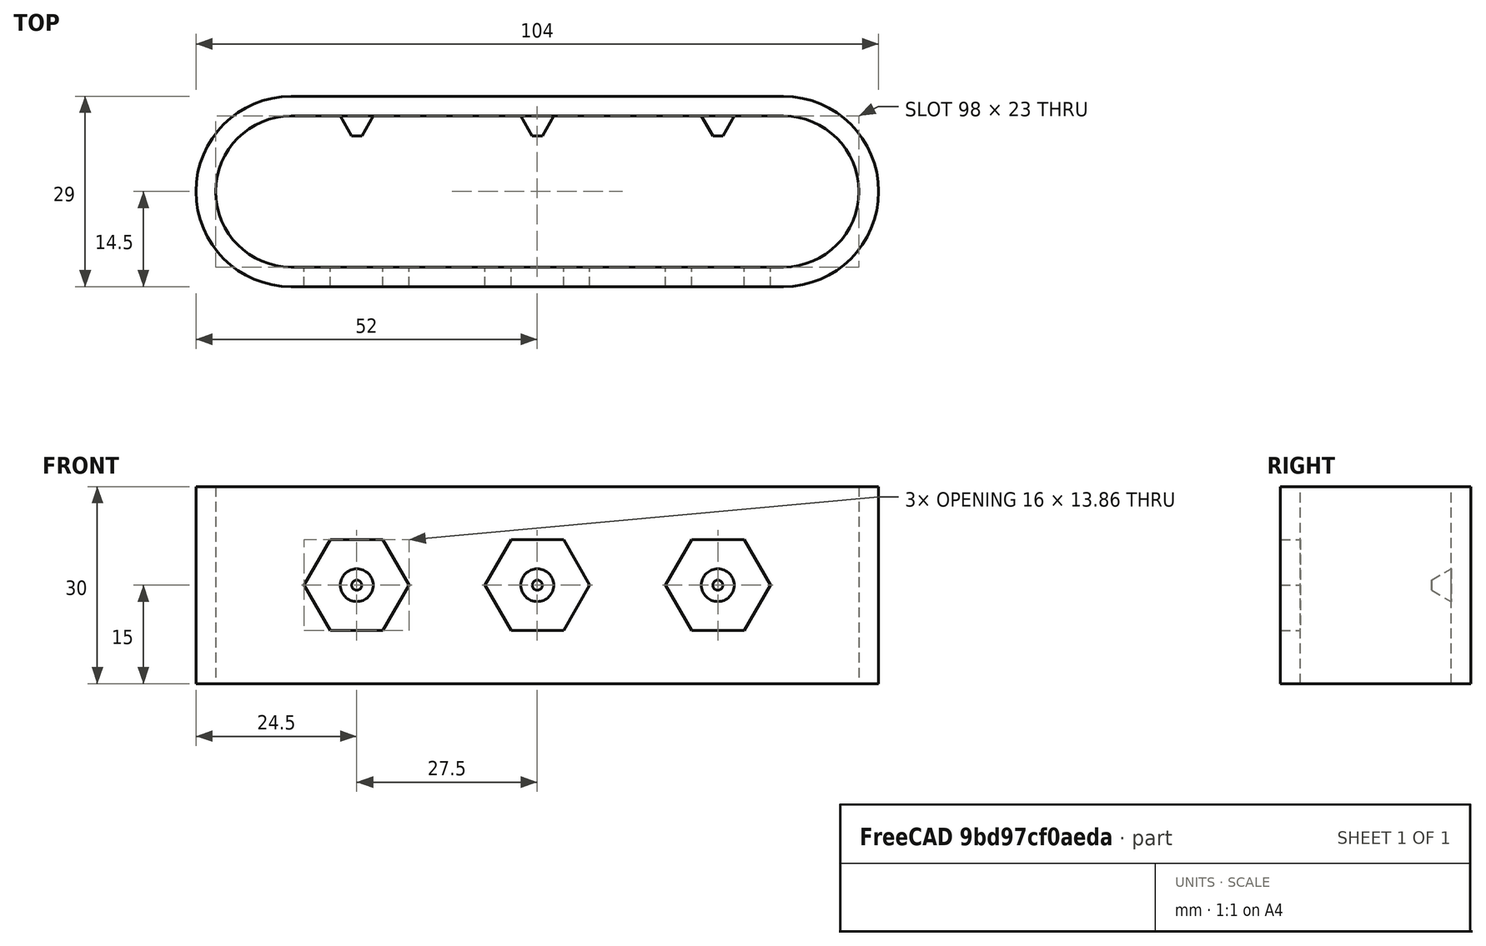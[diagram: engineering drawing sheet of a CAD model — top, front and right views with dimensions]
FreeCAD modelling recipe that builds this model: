
FCSTD DOCUMENT  (FreeCAD 0.17R13519 (Git))
Label: test004_stand2
License: All rights reserved
LicenseURL: http://en.wikipedia.org/wiki/All_rights_reserved
objects: Sketcher::SketchObject×3, PartDesign::Pad×2, PartDesign::LinearPattern×2, PartDesign::Pocket×1, PartDesign::Draft×1, PartDesign::Body×1, Fem::FemSolverObjectPython×1, Fem::FemMeshObject×1, Fem::ConstraintFixed×1, Fem::ConstraintForce×1, App::MaterialObjectPython×1, Fem::FemAnalysis×1
note: 13 computed .brp shape members not serialized (recipe doc carries the construction recipe); baked Part::Feature solids carry a one-line shape summary decoded from their .brp

FEATURE [Sketcher::SketchObject] Sketch
  MapMode = 5
  Support = -> [XY_Plane]
  sketch-geometry (8):
    g0: ArcOfCircle CenterX=0 CenterY=14.5 CenterZ=0 NormalX=0 NormalY=0 NormalZ=1 AngleXU=0 Radius=14.5 StartAngle=1.5708 EndAngle=4.71239
    g1: ArcOfCircle CenterX=75 CenterY=14.5 CenterZ=0 NormalX=0 NormalY=0 NormalZ=1 AngleXU=0 Radius=14.5 StartAngle=4.71239 EndAngle=7.85398
    g2: LineSegment StartX=0 StartY=0 StartZ=0 EndX=75 EndY=0 EndZ=0
    g3: LineSegment StartX=0 StartY=29 StartZ=0 EndX=75 EndY=29 EndZ=0
    g4: ArcOfCircle CenterX=0 CenterY=14.5 CenterZ=0 NormalX=0 NormalY=0 NormalZ=1 AngleXU=0 Radius=11.5 StartAngle=1.5708 EndAngle=4.71239
    g5: ArcOfCircle CenterX=75 CenterY=14.5 CenterZ=0 NormalX=0 NormalY=0 NormalZ=1 AngleXU=0 Radius=11.5 StartAngle=4.71239 EndAngle=7.85398
    g6: LineSegment StartX=0 StartY=3 StartZ=0 EndX=75 EndY=3 EndZ=0
    g7: LineSegment StartX=0 StartY=26 StartZ=0 EndX=75 EndY=26 EndZ=0
  constraints (18):
    c: Tangent(g0,g3) = 1.5708
    c: Tangent(g0,g2) = -1.5708
    c: Tangent(g2,g1) = -1.5708
    c: Tangent(g3,g1) = 1.5708
    c: Horizontal(g2)
    c: Equal(g0,g1)
    c: Tangent(g4,g7) = 1.5708
    c: Tangent(g4,g6) = -1.5708
    c: Tangent(g6,g5) = -1.5708
    c: Tangent(g7,g5) = 1.5708
    c: Horizontal(g6)
    c: Equal(g4,g5)
    c: Coincident(g0,g4)
    c: Coincident(g5,g1)
    c: Distance(g3) = 75
    c: DistanceY(g0,g0) = 29
    c: DistanceY(g4,g0) = 3
    c: Coincident(g-1,g0)
FEATURE [PartDesign::Pad] Pad
  Length = 30
  Length2 = 100
  Profile = -> Sketch
  Type = 0
FEATURE [Sketcher::SketchObject] Sketch001
  ExternalGeometry = -> [Pad]
  MapMode = 5
  Placement = pos=(0,0,0) rot=(1,0,0;1.5708rad)
  Support = -> [Pad]
  sketch-geometry (7):
    g0: LineSegment StartX=14 StartY=8.0718 StartZ=0 EndX=18 EndY=15 EndZ=0
    g1: LineSegment StartX=18 StartY=15 StartZ=0 EndX=14 EndY=21.9282 EndZ=0
    g2: LineSegment StartX=14 StartY=21.9282 StartZ=0 EndX=6 EndY=21.9282 EndZ=0
    g3: LineSegment StartX=6 StartY=21.9282 StartZ=0 EndX=2 EndY=15 EndZ=0
    g4: LineSegment StartX=2 StartY=15 StartZ=0 EndX=6 EndY=8.0718 EndZ=0
    g5: LineSegment StartX=6 StartY=8.0718 StartZ=0 EndX=14 EndY=8.0718 EndZ=0
    g6: Circle [constr] CenterX=10 CenterY=15 CenterZ=0 NormalX=0 NormalY=0 NormalZ=1 AngleXU=0 Radius=8
  constraints (17):
    c: Coincident(g0,g1)
    c: Coincident(g1,g2)
    c: Coincident(g2,g3)
    c: Coincident(g3,g4)
    c: Coincident(g4,g5)
    c: Coincident(g5,g0)
    c: Equal(g0, g1-g5) x5
    c: PointOnObject(g0,g6)
    c: PointOnObject(g1,g6)
    c: PointOnObject(g2,g6)
    c: PointOnObject(g3,g6)
    c: PointOnObject(g4,g6)
    c: PointOnObject(g5,g6)
    c: Horizontal(g5)
    c: Distance(g6,g-4) = 15
    c: Distance(g6,g-3) = 10
    c: Radius(g6) = 8
FEATURE [PartDesign::Pocket] Pocket
  BaseFeature = -> Pad
  Length = 3
  Length2 = 100
  Profile = -> Sketch001
  Type = 0
FEATURE [PartDesign::LinearPattern] LinearPattern
  BaseFeature = -> Pocket
  Direction = -> Sketch001 [H_Axis]
  Length = 55
  Occurrences = 3
  Originals = -> [Pocket]
FEATURE [Sketcher::SketchObject] Sketch002
  ExternalGeometry = -> [LinearPattern]
  MapMode = 5
  Placement = pos=(0,26,0) rot=(1,0,0;1.5708rad)
  Support = -> [LinearPattern]
  sketch-geometry (1):
    g0: Circle CenterX=10 CenterY=15 CenterZ=0 NormalX=0 NormalY=0 NormalZ=1 AngleXU=0 Radius=2.5
  constraints (3):
    c: Distance(g0,g-3) = 15
    c: Distance(g0,g-4) = 10
    c: Radius(g0) = 2.5
FEATURE [PartDesign::Pad] Pad001
  BaseFeature = -> LinearPattern
  Length = 3
  Length2 = 100
  Profile = -> Sketch002
  Type = 0
FEATURE [PartDesign::LinearPattern] LinearPattern001
  BaseFeature = -> Pad001
  Direction = -> Sketch002 [H_Axis]
  Length = 55
  Occurrences = 3
  Originals = -> [Pad001]
FEATURE [PartDesign::Draft] Draft
  Angle = 30
  Base = -> LinearPattern001 [Face30,Face31,Face29]
  BaseFeature = -> LinearPattern001
  NeutralPlane = -> LinearPattern001 [Face25]
  Reversed = true
FEATURE [PartDesign::Body] Body
  Group = -> [Sketch,Pad,Sketch001,Pocket,LinearPattern,Sketch002,Pad001,LinearPattern001,Draft]
  Origin = -> Origin
  Tip = -> Draft
FEATURE [Fem::FemSolverObjectPython] CalculiXccxTools  # FEM object (typed FeaturePython)
  AnalysisType = 0
  BeamShellResultOutput3D = false
  EigenmodeHighLimit = 1000000
  EigenmodeLowLimit = 0
  EigenmodesCount = 10
  GeometricalNonlinearity = 0
  IterationsControlParameterCutb = 0.25,0.5,0.75,0.85,,,1.5,
  IterationsControlParameterIter = 4,8,9,200,10,400,,200,,
  IterationsControlParameterTimeUse = false
  IterationsThermoMechMaximum = 2000
  IterationsUserDefinedIncrementations = false
  IterationsUserDefinedTimeStepLength = false
  MaterialNonlinearity = 0
  MatrixSolverType = 0
  SplitInputWriter = false
  ThermoMechSteadyState = true
  TimeEnd = 1
  TimeInitialStep = 0.01
FEATURE [Fem::FemMeshObject] Body_Mesh
FEATURE [Fem::ConstraintFixed] FemConstraintFixed
  NormalDirection = (0,1,0)
  Normals = (16) [(1.75e-15,1,0),(1.75e-15,1,0),(1.75e-15,1,0),(1.75e-15,1,0),(1.75e-15,1,0),(1.75e-15,1,0),(1.75e-15,1,0),(1.75e-15,1,0),(1.75e-15,1,0),(1.75e-15,1,0),+6 more]
  Points = (16) [(9.74e-15,29,30),(25,29,30),(50,29,30),(75,29,30),(9.74e-15,29,20),(25,29,20),(50,29,20),(75,29,20),(9.74e-15,29,10),(25,29,10),(50,29,10),(75,29,10),+4 more]
  References = -> [Draft]
  Scale = 6
FEATURE [Fem::ConstraintForce] FemConstraintForce
  DirectionVector = (0,-1,0)
  Force = 1
  NormalDirection = (0,-1,0)
  Points = (16) [(3.194e-14,0,30),(25,0,30),(50,0,30),(75,0,30),(3.194e-14,0,20),(25,0,20),(50,0,20),(75,0,20),(3.194e-14,0,10),(25,0,10),(50,0,10),(75,0,10),+4 more]
  References = -> [Draft]
  Scale = 6
FEATURE [App::MaterialObjectPython] SolidMaterial  # material (typed FeaturePython)
  Category = 0
  Material = Density=7900.0 kg/m^3,Description=Standard steel material for CalculiX sample calculations,Father=Metal,Name=CalculiX-Steel,PoissonRatio=0.3,+4 more (map truncated)
FEATURE [Fem::FemAnalysis] Analysis
  Group = -> [CalculiXccxTools,Body_Mesh,FemConstraintFixed,FemConstraintForce,SolidMaterial]
